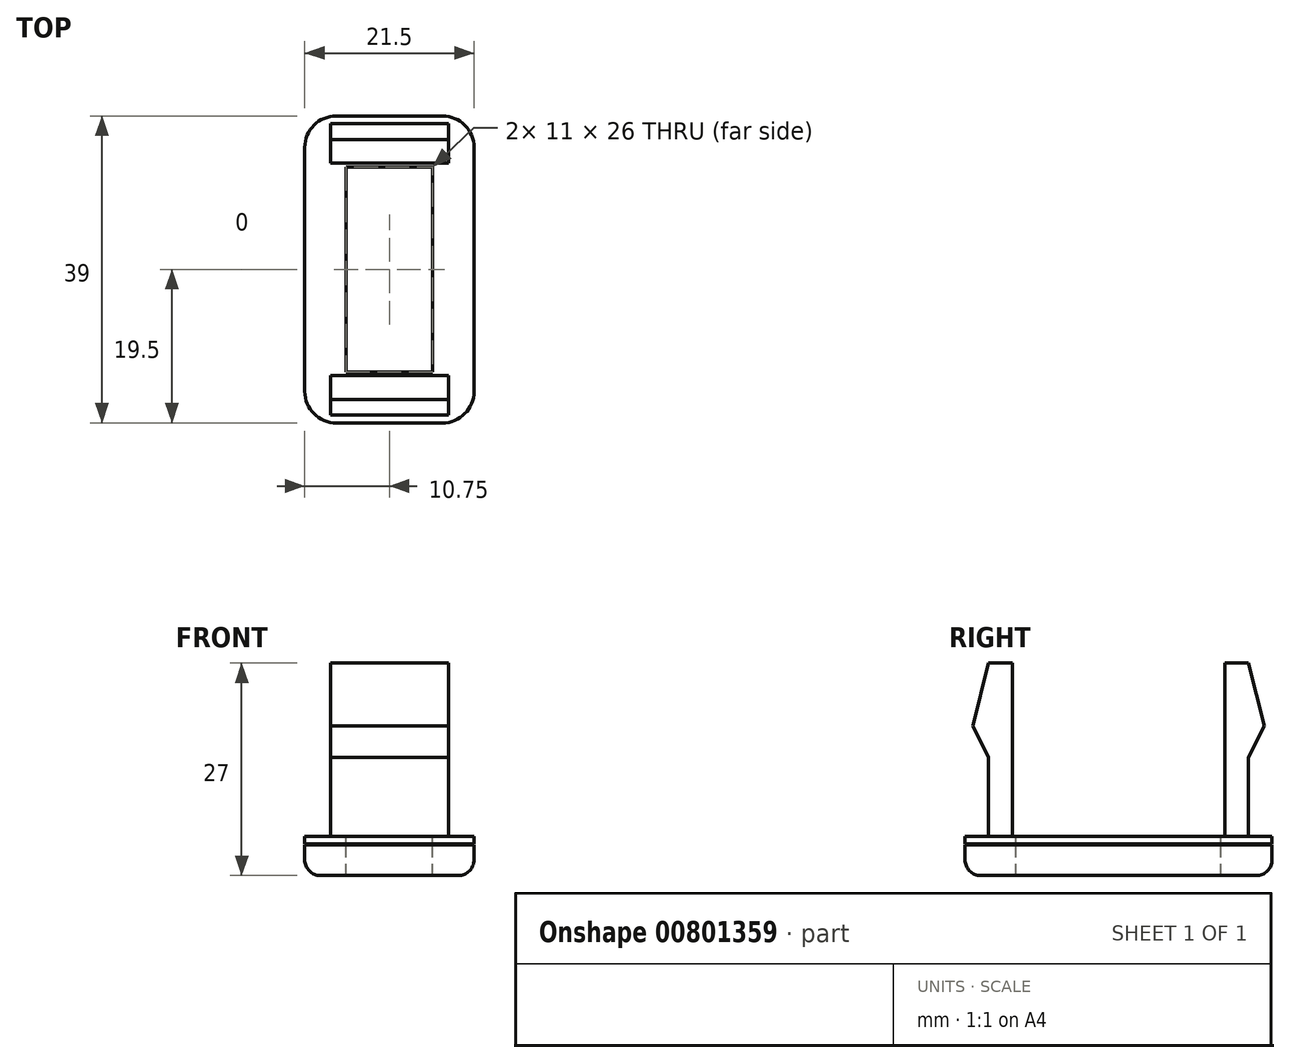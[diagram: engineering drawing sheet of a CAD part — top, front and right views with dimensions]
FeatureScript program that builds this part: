
annotation { "Feature Type Name" : "Feature", "Feature Type Description" : "" }
export const myFeature = defineFeature(function(context is Context, id is Id, definition is map)
    precondition{}
    {
        {
            var Q0;
            Q0=qCreatedBy(makeId("Top.planeOp"),FACE);
            var sketch = newSketch(context, id + "F0", { "sketchPlane" : qUnion([Q0])});
            skLineSegment(sketch, "E0.bottom", {"start": v(0, 0) * mm, "end": v(21.5, 0) * mm});
            skLineSegment(sketch, "E0.top", {"start": v(0, 39) * mm, "end": v(21.5, 39) * mm});
            skLineSegment(sketch, "E0.left", {"start": v(0, 0) * mm, "end": v(0, 39) * mm});
            skLineSegment(sketch, "E0.right", {"start": v(21.5, 0) * mm, "end": v(21.5, 39) * mm});
            skSolve(sketch);
        }
        {
            var Q0;
            Q0=makeQuery(id+"F0.imprint","IMPRINT",FACE,{"disambiguationData":[TD([[makeQuery(id+"F0.imprint","IMPRINT",EDGE,{"derivedFrom":sQuery(id+"F0.wireOp",EDGE,"E0.bottom")}),1.0]])]});
            extrude(context, id + "F1", {"entities" : qUnion([Q0]), "depth" : 5 * mm, "offsetDistance" : 25 * mm});
        }
        {
            var Q0;
            Q0=makeQuery(id+"F1.opExtrude","CAP_FACE",FACE,{"disambiguationData":[OSD([sQuery(id+"F0.wireOp",EDGE,"E0.bottom"),sQuery(id+"F0.wireOp",EDGE,"E0.top"),sQuery(id+"F0.wireOp",EDGE,"E0.left"),sQuery(id+"F0.wireOp",EDGE,"E0.right")])],"isStart":false});
            var sketch = newSketch(context, id + "F2", { "sketchPlane" : qUnion([Q0])});
            skLineSegment(sketch, "E1.bottom", {"start": v(3.25, 36) * mm, "end": v(18.25, 36) * mm});
            skLineSegment(sketch, "E1.top", {"start": v(3.25, 33) * mm, "end": v(18.25, 33) * mm});
            skLineSegment(sketch, "E1.left", {"start": v(3.25, 36) * mm, "end": v(3.25, 33) * mm});
            skLineSegment(sketch, "E1.right", {"start": v(18.25, 36) * mm, "end": v(18.25, 33) * mm});
            skLineSegment(sketch, "E2.bottom", {"start": v(3.25, 6) * mm, "end": v(18.25, 6) * mm});
            skLineSegment(sketch, "E2.top", {"start": v(3.25, 3) * mm, "end": v(18.25, 3) * mm});
            skLineSegment(sketch, "E2.left", {"start": v(3.25, 6) * mm, "end": v(3.25, 3) * mm});
            skLineSegment(sketch, "E2.right", {"start": v(18.25, 6) * mm, "end": v(18.25, 3) * mm});
            skSolve(sketch);
        }
        {
            var Q0;
            Q0=makeQuery(id+"F2.imprint","IMPRINT",FACE,{"disambiguationData":[TD([[makeQuery(id+"F2.imprint","IMPRINT",EDGE,{"derivedFrom":sQuery(id+"F2.wireOp",EDGE,"E1.bottom")}),-1.0]])]});
            var Q1;
            Q1=makeQuery(id+"F2.imprint","IMPRINT",FACE,{"disambiguationData":[TD([[makeQuery(id+"F2.imprint","IMPRINT",EDGE,{"derivedFrom":sQuery(id+"F2.wireOp",EDGE,"E2.bottom")}),-1.0]])]});
            extrude(context, id + "F3", {"entities" : qUnion([Q0, Q1]), "operationType" : NewBodyOperationType.ADD, "depth" : 22 * mm, "offsetDistance" : 25 * mm});
        }
        {
            var Q0;
            Q0=makeQuery(id+"F3.opExtrude","SWEPT_FACE",FACE,{"disambiguationData":[OSD([sQuery(id+"F2.wireOp",EDGE,"E2.left")])]});
            var sketch = newSketch(context, id + "F4", { "sketchPlane" : qUnion([Q0])});
            skLineSegment(sketch, "E3", {"start": v(-3, 27) * mm, "end": v(-1, 19) * mm});
            skLineSegment(sketch, "E4", {"start": v(-1, 19) * mm, "end": v(-3, 15) * mm});
            skLineSegment(sketch, "E5", {"start": v(-3, 15) * mm, "end": v(-3, 27) * mm});
            skLineSegment(sketch, "E6", {"start": v(-36, 27) * mm, "end": v(-36, 15) * mm});
            skLineSegment(sketch, "E7", {"start": v(-36, 15) * mm, "end": v(-38, 19) * mm});
            skLineSegment(sketch, "E8", {"start": v(-38, 19) * mm, "end": v(-36, 27) * mm});
            skSolve(sketch);
        }
        {
            var Q0;
            Q0=makeQuery(id+"F4.imprint","IMPRINT",FACE,{"disambiguationData":[TD([[makeQuery(id+"F4.imprint","IMPRINT",EDGE,{"derivedFrom":sQuery(id+"F4.wireOp",EDGE,"E6")}),-1.0]])]});
            var Q1;
            Q1=makeQuery(id+"F4.imprint","IMPRINT",FACE,{"disambiguationData":[TD([[makeQuery(id+"F4.imprint","IMPRINT",EDGE,{"derivedFrom":sQuery(id+"F4.wireOp",EDGE,"E3")}),-1.0]])]});
            extrude(context, id + "F5", {"entities" : qUnion([Q0, Q1]), "operationType" : NewBodyOperationType.ADD, "oppositeDirection" : true, "depth" : 15 * mm, "offsetDistance" : 25 * mm});
        }
        {
            var Q0;
            Q0=makeQuery(id+"F1.opExtrude","SWEPT_EDGE",EDGE,{"disambiguationData":[OSD([sQuery(id+"F0.wireOp",EDGE,"E0.top"),sQuery(id+"F0.wireOp",EDGE,"E0.left")])]});
            var Q1;
            Q1=makeQuery(id+"F1.opExtrude","SWEPT_EDGE",EDGE,{"disambiguationData":[OSD([sQuery(id+"F0.wireOp",EDGE,"E0.bottom"),sQuery(id+"F0.wireOp",EDGE,"E0.left")])]});
            var Q2;
            Q2=makeQuery(id+"F1.opExtrude","SWEPT_EDGE",EDGE,{"disambiguationData":[OSD([sQuery(id+"F0.wireOp",EDGE,"E0.bottom"),sQuery(id+"F0.wireOp",EDGE,"E0.right")])]});
            var Q3;
            Q3=makeQuery(id+"F1.opExtrude","SWEPT_EDGE",EDGE,{"disambiguationData":[OSD([sQuery(id+"F0.wireOp",EDGE,"E0.top"),sQuery(id+"F0.wireOp",EDGE,"E0.right")])]});
            fillet(context, id + "F6", {"entities" : qUnion([Q0, Q1, Q2, Q3]), "radius" : 4 * mm, "tangentPropagation" : true, "allowEdgeOverflow" : false});
        }
        {
            var Q0;
            Q0=makeQuery(id+"F1.opExtrude","CAP_FACE",FACE,{"disambiguationData":[OSD([sQuery(id+"F0.wireOp",EDGE,"E0.bottom"),sQuery(id+"F0.wireOp",EDGE,"E0.top"),sQuery(id+"F0.wireOp",EDGE,"E0.left"),sQuery(id+"F0.wireOp",EDGE,"E0.right")])],"isStart":true});
            fillet(context, id + "F7", {"entities" : qUnion([Q0]), "radius" : 2 * mm, "tangentPropagation" : true, "allowEdgeOverflow" : false});
        }
        {
            var Q0;
            Q0=makeQuery(id+"F1.opExtrude","CAP_FACE",FACE,{"disambiguationData":[OSD([sQuery(id+"F0.wireOp",EDGE,"E0.bottom"),sQuery(id+"F0.wireOp",EDGE,"E0.top"),sQuery(id+"F0.wireOp",EDGE,"E0.left"),sQuery(id+"F0.wireOp",EDGE,"E0.right")])],"isStart":false});
            var sketch = newSketch(context, id + "F8", { "sketchPlane" : qUnion([Q0])});
            skLineSegment(sketch, "E9.bottom", {"start": v(5.25, 32.5) * mm, "end": v(16.25, 32.5) * mm});
            skLineSegment(sketch, "E9.top", {"start": v(5.25, 6.5) * mm, "end": v(16.25, 6.5) * mm});
            skLineSegment(sketch, "E9.left", {"start": v(5.25, 32.5) * mm, "end": v(5.25, 6.5) * mm});
            skLineSegment(sketch, "E9.right", {"start": v(16.25, 32.5) * mm, "end": v(16.25, 6.5) * mm});
            skSolve(sketch);
        }
        {
            var Q0;
            Q0=makeQuery(id+"F8.imprint","IMPRINT",FACE,{"disambiguationData":[TD([[makeQuery(id+"F8.imprint","IMPRINT",EDGE,{"derivedFrom":sQuery(id+"F8.wireOp",EDGE,"E9.bottom")}),-1.0]])]});
            extrude(context, id + "F9", {"entities" : qUnion([Q0]), "operationType" : NewBodyOperationType.REMOVE, "oppositeDirection" : true, "depth" : 6 * mm, "offsetDistance" : 25 * mm});
        }
        {
            var Q0;
            Q0=makeQuery(id+"F1.opExtrude","SWEPT_FACE",FACE,{"disambiguationData":[OSD([sQuery(id+"F0.wireOp",EDGE,"E0.right")])]});
            var sketch = newSketch(context, id + "F10", { "sketchPlane" : qUnion([Q0])});
            skLineSegment(sketch, "E10.bottom", {"start": v(-1.17, 4) * mm, "end": v(48.83, 4) * mm});
            skLineSegment(sketch, "E10.top", {"start": v(-1.17, 3.9) * mm, "end": v(48.83, 3.9) * mm});
            skLineSegment(sketch, "E10.left", {"start": v(-1.17, 4) * mm, "end": v(-1.17, 3.9) * mm});
            skLineSegment(sketch, "E10.right", {"start": v(48.83, 4) * mm, "end": v(48.83, 3.9) * mm});
            skSolve(sketch);
        }
        {
            var Q0;
            {var subQ0=sQuery(id+"F10.wireOp",EDGE,"E10.bottom");var subQ1=sQuery(id+"F0.wireOp",EDGE,"E0.right");var subQ2=makeQuery(id+"F1.opExtrude","SWEPT_FACE",FACE,{"disambiguationData":[OSD([subQ1])]});var subQ3=makeQuery(id+"F6.opFillet","BLEND_EDGE",EDGE,{"blendedFrom":[makeQuery(id+"F1.opExtrude","SWEPT_EDGE",EDGE,{"disambiguationData":[OSD([sQuery(id+"F0.wireOp",EDGE,"E0.bottom"),subQ1])]}),subQ2],"blendedInto":[subQ2]});var subQ4=makeQuery(id+"F10.imprint","INTERSECT",VERTEX,{"derivedFrom":[subQ3,subQ0]});Q0=makeQuery(id+"F10.imprint","IMPRINT",FACE,{"disambiguationData":[TD([[makeQuery(id+"F10.imprint","IMPRINT",EDGE,{"disambiguationData":[TD([[subQ4,-1.0]])],"derivedFrom":subQ0}),-1.0]])]});}
            var Q1;
            {var subQ0=sQuery(id+"F10.wireOp",EDGE,"E10.left");Q1=makeQuery(id+"F10.imprint","IMPRINT",FACE,{"disambiguationData":[TD([[makeQuery(id+"F10.imprint","IMPRINT",EDGE,{"derivedFrom":subQ0}),1.0]])]});}
            var Q2;
            {var subQ0=sQuery(id+"F10.wireOp",EDGE,"E10.right");Q2=makeQuery(id+"F10.imprint","IMPRINT",FACE,{"disambiguationData":[TD([[makeQuery(id+"F10.imprint","IMPRINT",EDGE,{"derivedFrom":subQ0}),-1.0]])]});}
            extrude(context, id + "F11", {"entities" : qUnion([Q0, Q1, Q2]), "operationType" : NewBodyOperationType.REMOVE, "oppositeDirection" : true, "depth" : 40 * mm, "offsetDistance" : 25 * mm});
        }
    });
